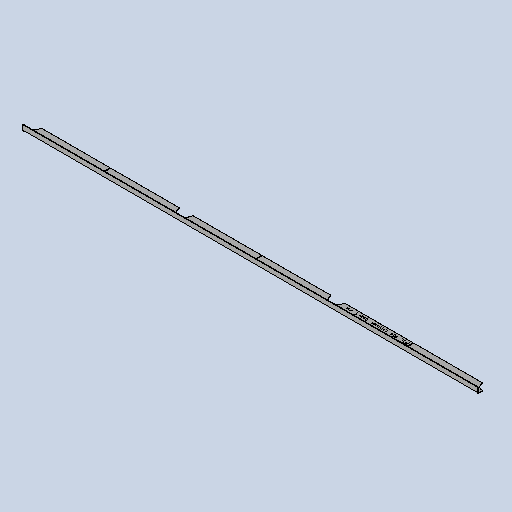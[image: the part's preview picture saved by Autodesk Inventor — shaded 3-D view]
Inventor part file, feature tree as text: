
AUTODESK INVENTOR PART (.ipt)
format: ipt  version: 2025 (Build 290162010, 162A)  size: 323,072 bytes
history: native  units: mm
features: sketch x6, other x5, sheet_metal_op x4, extrude x3, mirror x2, pattern_linear x1, projected_geometry x1
ambient origin geometry x8: Origin, YZ Plane, XZ Plane, XY Plane, X Axis, Y Axis, Z Axis, Center Point
bodies: Solid1 (feature_tree)
feature tree (22):
  sheet_metal_op  "Face1"
  sheet_metal_op  "Flange1"
  extrude  "Extrusion1"  Depth=39.0mm
  pattern_linear  "Rectangular Pattern1"  Count1=2 Spacing1=90.0deg
  extrude  "Extrusion2"  Depth=8.0mm
  mirror  "Mirror1"
  extrude  "Extrusion3"  Depth=2.0mm
  mirror  "Mirror2"
  other  "Mark1"
  other  "A-Side Definition"
  sketch  "Sketch1"  dims[d0=1500.0mm d1=39.0mm]
  other  "Plate1"
  sketch  "Sketch2"  dims[d2=2.0mm]
  other  "Plate2"
  sheet_metal_op  "Bend1"
  sheet_metal_op  "Corner1"
  sketch  "Sketch5"  dims[d3=2.0mm]
  sketch  "Sketch6"  dims[d4=1.0mm]
  sketch  "Sketch7"  dims[d5=4.0mm]
  projected_geometry  "Projected Loop3"
  sketch  "Sketch8"  dims[d6=2.75mm d7=20.0mm d8=90.0deg d9=2.75mm d10=8.0mm d11=2.0mm d12=2.75mm d15=0.0mm d16=0.0mm d18=2.0mm d21=30.0mm d23=500.0mm d24=45.0mm d25=30.0mm d26=0.0mm d27=2.0mm d28=20.0mm d29=100.0mm d30=10.0mm d31=10.0mm d32=20.0mm d33=0.0mm d34=0.0mm d35=200.0mm d36=12.0mm d39=5.0mm d40=5.0mm]
  other  "Definition1"
